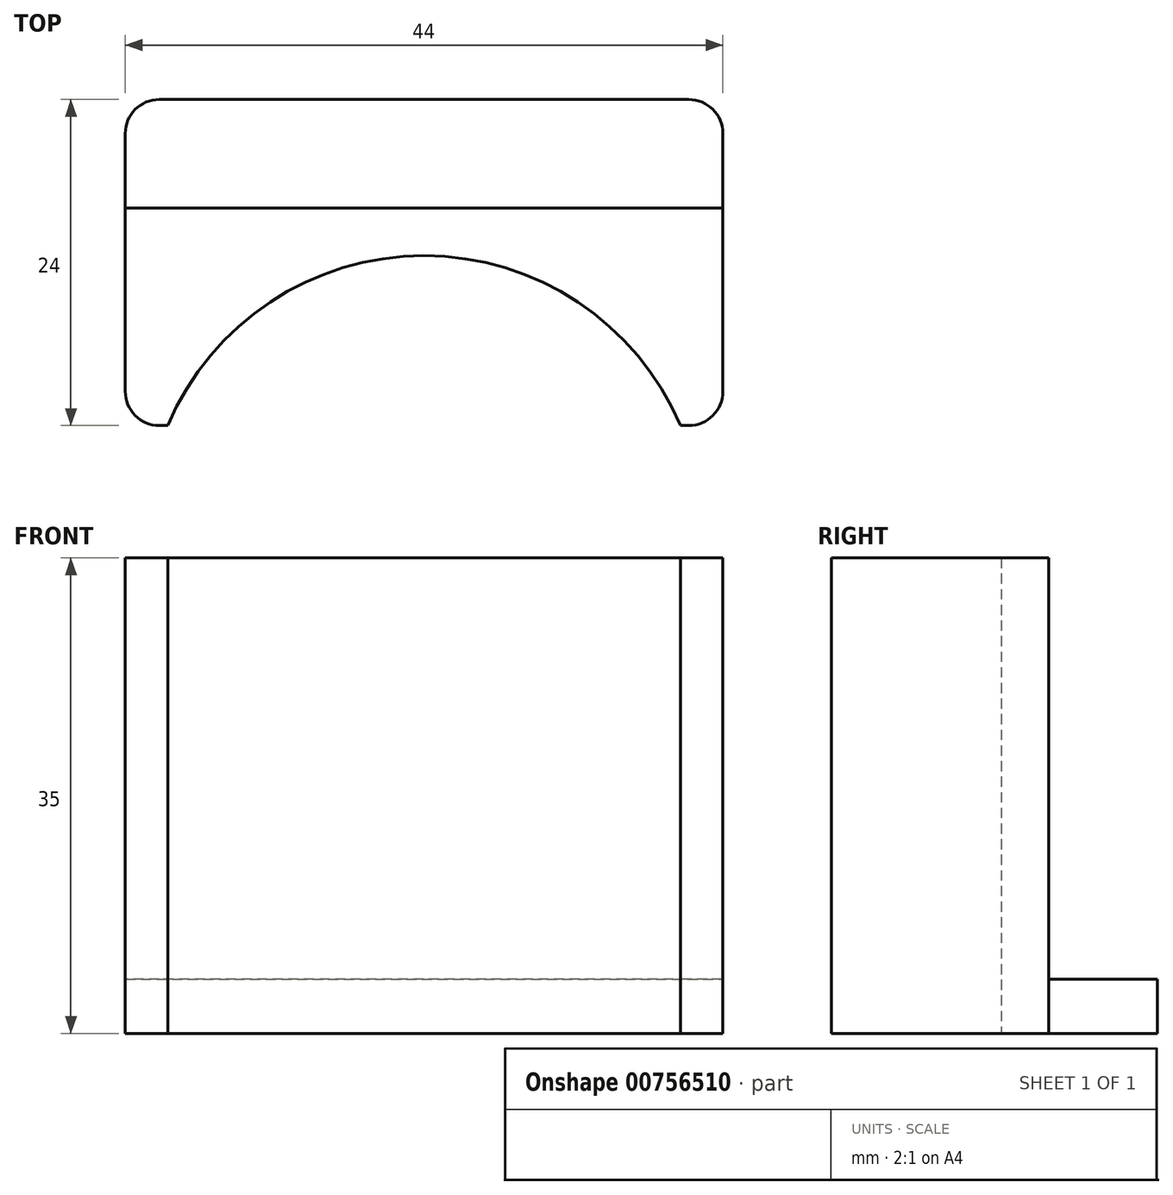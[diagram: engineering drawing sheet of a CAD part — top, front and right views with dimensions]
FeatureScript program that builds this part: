
annotation { "Feature Type Name" : "Feature", "Feature Type Description" : "" }
export const myFeature = defineFeature(function(context is Context, id is Id, definition is map)
    precondition{}
    {
        {
            var Q0;
            Q0=qCreatedBy(makeId("Top.planeOp"),FACE);
            var sketch = newSketch(context, id + "F0", { "sketchPlane" : qUnion([Q0])});
            skCircle(sketch, "E0", {"center": v(0, 0) * mm, "radius": 20.5 * mm});
            skSolve(sketch);
        }
        {
            var Q0;
            Q0 = qSketchRegion(id + "F0", true);
            extrude(context, id + "F1", {"entities" : qUnion([Q0]), "depth" : 50 * mm, "offsetDistance" : 25 * mm});
        }
        {
            var Q0;
            Q0=qCreatedBy(makeId("Top.planeOp"),FACE);
            var sketch = newSketch(context, id + "F2", { "sketchPlane" : qUnion([Q0])});
            skLineSegment(sketch, "E1", {"start": v(0, 0) * mm, "end": v(0, 8) * mm});
            skLineSegment(sketch, "E2", {"start": v(0, 8) * mm, "end": v(22, 8) * mm});
            skLineSegment(sketch, "E3", {"start": v(22, 8) * mm, "end": v(22, 24) * mm});
            skLineSegment(sketch, "E4", {"start": v(22, 24) * mm, "end": v(-22, 24) * mm});
            skLineSegment(sketch, "E5", {"start": v(-22, 24) * mm, "end": v(-22, 8) * mm});
            skLineSegment(sketch, "E6", {"start": v(-22, 8) * mm, "end": v(0, 8) * mm});
            skSolve(sketch);
        }
        {
            var Q0;
            Q0 = qSketchRegion(id + "F2", true);
            extrude(context, id + "F3", {"entities" : qUnion([Q0]), "depth" : 35 * mm, "offsetDistance" : 25 * mm});
        }
        {
            var Q0;
            Q0=makeQuery(id+"F1.opExtrude","SWEPT_BODY",BODY,{"disambiguationData":[OSD([sQuery(id+"F0.wireOp",EDGE,"E0")])]});
            var Q1;
            Q1=makeQuery(id+"F3.opExtrude","SWEPT_BODY",BODY,{"disambiguationData":[OSD([sQuery(id+"F2.wireOp",EDGE,"E2"),sQuery(id+"F2.wireOp",EDGE,"E3"),sQuery(id+"F2.wireOp",EDGE,"E4"),sQuery(id+"F2.wireOp",EDGE,"E5"),sQuery(id+"F2.wireOp",EDGE,"E6")])]});
            booleanBodies(context, id + "F4", {"operationType" : BooleanOperationType.SUBTRACTION, "tools" : qUnion([Q0]), "targets" : qUnion([Q1])});
        }
        {
            var Q0;
            Q0=qCreatedBy(makeId("Top.planeOp"),FACE);
            var sketch = newSketch(context, id + "F5", { "sketchPlane" : qUnion([Q0])});
            skLineSegment(sketch, "E7", {"start": v(0, 0) * mm, "end": v(22, 0) * mm});
            skLineSegment(sketch, "E8", {"start": v(22, 0) * mm, "end": v(22, 24) * mm});
            skLineSegment(sketch, "E9", {"start": v(22, 24) * mm, "end": v(22, 32) * mm});
            skLineSegment(sketch, "E10", {"start": v(22, 32) * mm, "end": v(-22, 32) * mm});
            skLineSegment(sketch, "E11", {"start": v(-22, 32) * mm, "end": v(-22, 24) * mm});
            skLineSegment(sketch, "E12", {"start": v(-22, 24) * mm, "end": v(22, 24) * mm});
            skSolve(sketch);
        }
        {
            var Q0;
            Q0 = qSketchRegion(id + "F5", true);
            extrude(context, id + "F6", {"entities" : qUnion([Q0]), "depth" : 4 * mm, "offsetDistance" : 25 * mm});
        }
        {
            var Q0;
            Q0=makeQuery(id+"F3.opExtrude","SWEPT_EDGE",EDGE,{"disambiguationData":[OSD([sQuery(id+"F2.wireOp",EDGE,"E5"),sQuery(id+"F2.wireOp",EDGE,"E6")])]});
            var Q1;
            Q1=makeQuery(id+"F3.opExtrude","SWEPT_EDGE",EDGE,{"disambiguationData":[OSD([sQuery(id+"F2.wireOp",EDGE,"E2"),sQuery(id+"F2.wireOp",EDGE,"E3")])]});
            var Q2;
            Q2=makeQuery(id+"F6.opExtrude","SWEPT_EDGE",EDGE,{"disambiguationData":[OSD([sQuery(id+"F5.wireOp",EDGE,"E10"),sQuery(id+"F5.wireOp",EDGE,"E11")])]});
            var Q3;
            Q3=makeQuery(id+"F6.opExtrude","SWEPT_EDGE",EDGE,{"disambiguationData":[OSD([sQuery(id+"F5.wireOp",EDGE,"E9"),sQuery(id+"F5.wireOp",EDGE,"E10")])]});
            fillet(context, id + "F7", {"entities" : qUnion([Q0, Q1, Q2, Q3]), "radius" : 2.5 * mm, "tangentPropagation" : true, "allowEdgeOverflow" : false});
        }
        {
            var Q0;
            Q0=qCreatedBy(makeId("Front.planeOp"),FACE);
            var sketch = newSketch(context, id + "F8", { "sketchPlane" : qUnion([Q0])});
            skLineSegment(sketch, "E13", {"start": v(0, 0) * mm, "end": v(0, 19.26) * mm});
            skCircle(sketch, "E14", {"center": v(0, 19.26) * mm, "radius": 5.3 * mm});
            skSolve(sketch);
        }
        {
            var Q0;
            Q0=makeQuery(id+"F8.imprint","IMPRINT",FACE,{"disambiguationData":[TD([[makeQuery(id+"F8.imprint","IMPRINT",EDGE,{"derivedFrom":sQuery(id+"F8.wireOp",EDGE,"E14")}),1.0]])]});
            extrude(context, id + "F9", {"entities" : qUnion([Q0]), "depth" : 2.1 * mm, "offsetDistance" : 25 * mm});
        }
        {
            var Q0;
            Q0=makeQuery(id+"F9.opExtrude","SWEPT_BODY",BODY,{"disambiguationData":[OSD([sQuery(id+"F8.wireOp",EDGE,"E14")])]});
            transform(context, id + "F10", {"entities" : qUnion([Q0]), "transformType" : TransformType.TRANSLATION_3D, "dx" : 0 * mm, "dy" : 24 * mm, "dz" : 0 * mm, "makeCopy" : false});
        }
        {
            var Q0;
            Q0=makeQuery(id+"F9.opExtrude","SWEPT_BODY",BODY,{"disambiguationData":[OSD([sQuery(id+"F8.wireOp",EDGE,"E14")])]});
            var Q1;
            Q1=makeQuery(id+"F6.opExtrude","SWEPT_BODY",BODY,{"disambiguationData":[OSD([sQuery(id+"F5.wireOp",EDGE,"E9"),sQuery(id+"F5.wireOp",EDGE,"E10"),sQuery(id+"F5.wireOp",EDGE,"E11"),sQuery(id+"F5.wireOp",EDGE,"E12")])]});
            booleanBodies(context, id + "F11", {"operationType" : BooleanOperationType.SUBTRACTION, "tools" : qUnion([Q0]), "targets" : qUnion([Q1])});
        }
    });
